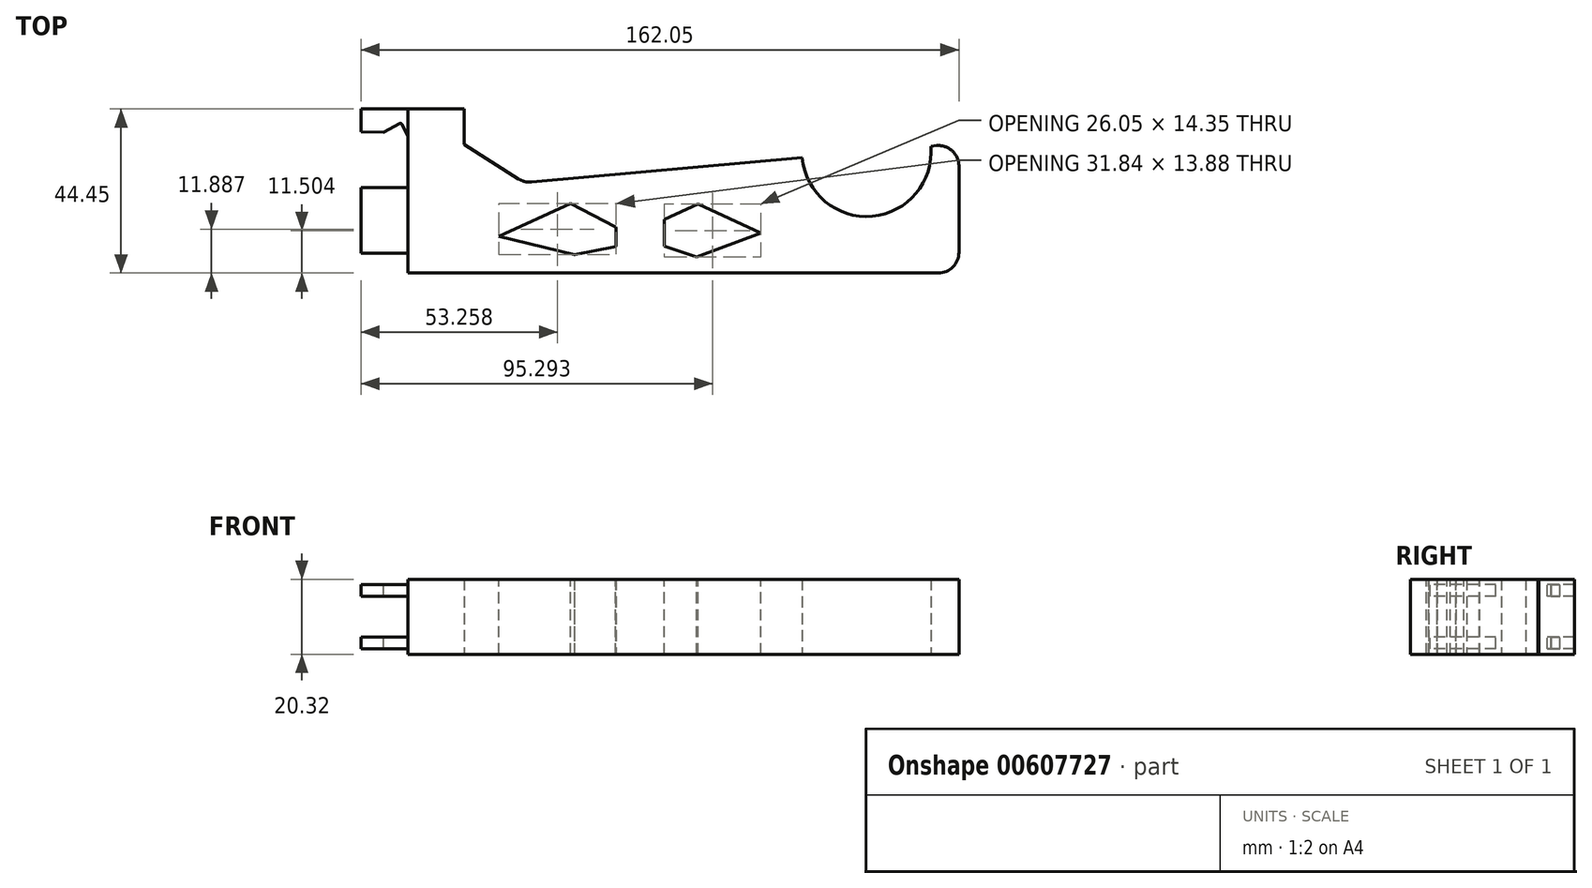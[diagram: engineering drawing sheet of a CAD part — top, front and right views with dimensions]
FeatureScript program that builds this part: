
annotation { "Feature Type Name" : "Feature", "Feature Type Description" : "" }
export const myFeature = defineFeature(function(context is Context, id is Id, definition is map)
    precondition{}
    {
        {
            var Q0;
            Q0=qCreatedBy(makeId("Top.planeOp"),FACE);
            var sketch = newSketch(context, id + "F0", { "sketchPlane" : qUnion([Q0])});
            skLineSegment(sketch, "E0", {"start": v(0, 0) * mm, "end": v(0, -44.45) * mm});
            skLineSegment(sketch, "E1", {"start": v(0, -44.45) * mm, "end": v(143.76, -44.45) * mm});
            skLineSegment(sketch, "E2", {"start": v(149.35, -38.86) * mm, "end": v(149.35, -15.5) * mm});
            skLineSegment(sketch, "E3", {"start": v(143.26, -9.94) * mm, "end": v(141.73, -10.08) * mm});
            skLineSegment(sketch, "E4", {"start": v(30.06, -18.98) * mm, "end": v(15.23, -9.62) * mm});
            skPoint(sketch, "E5", {"position": v(149.35, -9.4) * mm});
            skPoint(sketch, "E6", {"position": v(149.35, 0) * mm});
            skArc(sketch, "E7", {"start": v(106.9, -13.22) * mm, "mid": v(125.88, -29.07) * mm, "end": v(141.73, -10.08) * mm});
            skLineSegment(sketch, "E8.trimOffspring", {"start": v(106.9, -13.22) * mm, "end": v(33.55, -19.82) * mm});
            skPoint(sketch, "E9.visualSharp", {"position": v(31.66, -20) * mm});
            skArc(sketch, "E9.filletArc", {"start": v(30.06, -18.98) * mm, "mid": v(31.73, -19.69) * mm, "end": v(33.55, -19.82) * mm});
            skArc(sketch, "E10.filletArc", {"start": v(149.35, -15.5) * mm, "mid": v(147.53, -11.38) * mm, "end": v(143.26, -9.94) * mm});
            skPoint(sketch, "E11.visualSharp", {"position": v(149.35, -44.45) * mm});
            skArc(sketch, "E11.filletArc", {"start": v(143.76, -44.45) * mm, "mid": v(147.72, -42.81) * mm, "end": v(149.35, -38.86) * mm});
            skLineSegment(sketch, "E12", {"start": v(0, 0) * mm, "end": v(15.23, 0) * mm});
            skLineSegment(sketch, "E13", {"start": v(15.23, 0) * mm, "end": v(15.23, -9.62) * mm});
            skSolve(sketch);
        }
        {
            var Q0;
            Q0 = qSketchRegion(id + "F0", true);
            extrude(context, id + "F1", {"entities" : qUnion([Q0]), "depth" : 20.32 * mm, "offsetDistance" : 25.4 * mm});
        }
        {
            var Q0;
            Q0=makeQuery(id+"F1.opExtrude","SWEPT_FACE",FACE,{"disambiguationData":[OSD([sQuery(id+"F0.wireOp",EDGE,"E0")])]});
            var sketch = newSketch(context, id + "F2", { "sketchPlane" : qUnion([Q0])});
            skLineSegment(sketch, "E14", {"start": v(0, 10.16) * mm, "end": v(44.45, 10.16) * mm});
            skLineSegment(sketch, "E15.0", {"start": v(0, 4.6) * mm, "end": v(44.45, 4.6) * mm});
            skLineSegment(sketch, "E16.0", {"start": v(0, 1.43) * mm, "end": v(44.45, 1.43) * mm});
            skLineSegment(sketch, "E17.MirrorCS", {"start": v(0, 15.72) * mm, "end": v(44.45, 15.72) * mm});
            skLineSegment(sketch, "E18.MirrorCS", {"start": v(0, 18.9) * mm, "end": v(44.45, 18.9) * mm});
            skSolve(sketch);
        }
        {
            var Q0;
            Q0 = qSketchRegion(id + "F2", true);
            var Q1;
            {var subQ0=sQuery(id+"F2.wireOp",EDGE,"E15.0");Q1=makeQuery(id+"F2.imprint","IMPRINT",FACE,{"disambiguationData":[TD([[makeQuery(id+"F2.imprint","IMPRINT",EDGE,{"derivedFrom":subQ0}),-1.0]])]});}
            var Q2;
            {var subQ0=sQuery(id+"F2.wireOp",EDGE,"E17.MirrorCS");Q2=makeQuery(id+"F2.imprint","IMPRINT",FACE,{"disambiguationData":[TD([[makeQuery(id+"F2.imprint","IMPRINT",EDGE,{"derivedFrom":subQ0}),1.0]])]});}
            extrude(context, id + "F3", {"entities" : qUnion([Q0, Q1, Q2]), "operationType" : NewBodyOperationType.ADD, "depth" : 12.7 * mm, "offsetDistance" : 25.4 * mm});
        }
        {
            var Q0;
            Q0=makeQuery(id+"F3.opExtrude","SWEPT_FACE",FACE,{"disambiguationData":[OSD([sQuery(id+"F2.wireOp",EDGE,"E18.MirrorCS")])]});
            var sketch = newSketch(context, id + "F4", { "sketchPlane" : qUnion([Q0])});
            skLineSegment(sketch, "E19", {"start": v(-12.7, -21.26) * mm, "end": v(0, -21.26) * mm});
            skLineSegment(sketch, "E20.0", {"start": v(-12.7, -7.3) * mm, "end": v(0, -7.3) * mm});
            skLineSegment(sketch, "E21", {"start": v(-12.7, -21.26) * mm, "end": v(-12.7, -7.3) * mm});
            skLineSegment(sketch, "E22", {"start": v(0, -7.3) * mm, "end": v(0, -21.26) * mm});
            skLineSegment(sketch, "E23.0", {"start": v(-12.7, -39.04) * mm, "end": v(0, -39.04) * mm});
            skLineSegment(sketch, "E24", {"start": v(-12.7, -39.04) * mm, "end": v(-12.7, -44.45) * mm});
            skLineSegment(sketch, "E25", {"start": v(-12.23, -44.68) * mm, "end": v(0, -44.45) * mm});
            skLineSegment(sketch, "E26", {"start": v(0, -44.45) * mm, "end": v(0, -39.04) * mm});
            skLineSegment(sketch, "E27", {"start": v(0, 0) * mm, "end": v(-12.7, 0) * mm});
            skLineSegment(sketch, "E28", {"start": v(-12.7, 0) * mm, "end": v(-12.7, -6.22) * mm});
            skLineSegment(sketch, "E29", {"start": v(-12.7, -6.22) * mm, "end": v(-6.6, -6.28) * mm});
            skLineSegment(sketch, "E30", {"start": v(-6.6, -6.28) * mm, "end": v(-2.11, -3.97) * mm});
            skLineSegment(sketch, "E31", {"start": v(-1.6, -4.13) * mm, "end": v(0, -7.3) * mm});
            skPoint(sketch, "E32.visualSharp", {"position": v(-1.78, -3.8) * mm});
            skArc(sketch, "E32.filletArc", {"start": v(-1.6, -4.13) * mm, "mid": v(-1.83, -3.94) * mm, "end": v(-2.11, -3.97) * mm});
            skLineSegment(sketch, "E33", {"start": v(-12.7, -7.3) * mm, "end": v(-12.7, -6.22) * mm});
            skSolve(sketch);
        }
        {
            var Q0;
            Q0 = qSketchRegion(id + "F4", true);
            var Q1;
            Q1=makeQuery(id+"F4.imprint","IMPRINT",FACE,{"disambiguationData":[TD([[makeQuery(id+"F4.imprint","IMPRINT",EDGE,{"derivedFrom":sQuery(id+"F4.wireOp",EDGE,"E23.0")}),-1.0]])]});
            var Q2;
            Q2=makeQuery(id+"F3.opExtrude","SWEPT_FACE",FACE,{"disambiguationData":[OSD([sQuery(id+"F2.wireOp",EDGE,"E16.0")])]});
            extrude(context, id + "F5", {"entities" : qUnion([Q0, Q1]), "operationType" : NewBodyOperationType.REMOVE, "endBound" : BoundingType.UP_TO_SURFACE, "oppositeDirection" : true, "depth" : 25.4 * mm, "endBoundEntityFace" : qUnion([Q2]), "offsetDistance" : 25.4 * mm});
        }
        {
            var Q0;
            Q0=makeQuery(id+"F1.opExtrude","CAP_FACE",FACE,{"disambiguationData":[OSD([sQuery(id+"F0.wireOp",EDGE,"E0"),sQuery(id+"F0.wireOp",EDGE,"E1"),sQuery(id+"F0.wireOp",EDGE,"E2"),sQuery(id+"F0.wireOp",EDGE,"E3"),sQuery(id+"F0.wireOp",EDGE,"E4"),sQuery(id+"F0.wireOp",EDGE,"E7"),sQuery(id+"F0.wireOp",EDGE,"E8.trimOffspring"),sQuery(id+"F0.wireOp",EDGE,"E9.filletArc"),sQuery(id+"F0.wireOp",EDGE,"E10.filletArc"),sQuery(id+"F0.wireOp",EDGE,"E11.filletArc"),sQuery(id+"F0.wireOp",EDGE,"E12"),sQuery(id+"F0.wireOp",EDGE,"E13")])],"isStart":false});
            var sketch = newSketch(context, id + "F6", { "sketchPlane" : qUnion([Q0])});
            skLineSegment(sketch, "E34", {"start": v(24.64, -34.53) * mm, "end": v(44.12, -25.62) * mm});
            skLineSegment(sketch, "E35", {"start": v(44.12, -25.62) * mm, "end": v(60.43, -34.08) * mm});
            skLineSegment(sketch, "E36", {"start": v(60.43, -34.08) * mm, "end": v(78.7, -25.77) * mm});
            skLineSegment(sketch, "E37", {"start": v(78.7, -25.77) * mm, "end": v(95.62, -33.63) * mm});
            skLineSegment(sketch, "E38", {"start": v(95.62, -33.63) * mm, "end": v(78.25, -40.12) * mm});
            skLineSegment(sketch, "E39", {"start": v(78.25, -40.12) * mm, "end": v(60.43, -34.08) * mm});
            skLineSegment(sketch, "E40", {"start": v(24.64, -34.53) * mm, "end": v(45.18, -39.52) * mm});
            skLineSegment(sketch, "E41", {"start": v(45.18, -39.52) * mm, "end": v(65, -35.63) * mm});
            skLineSegment(sketch, "E42", {"start": v(56.48, -32.03) * mm, "end": v(56.48, -37.3) * mm});
            skLineSegment(sketch, "E43", {"start": v(56.48, -37.3) * mm, "end": v(69.57, -29.93) * mm});
            skLineSegment(sketch, "E44", {"start": v(69.57, -29.93) * mm, "end": v(69.57, -37.18) * mm});
            skSolve(sketch);
        }
        {
            var Q0;
            Q0=makeQuery(id+"F6.imprint","IMPRINT",FACE,{"disambiguationData":[TD([[makeQuery(id+"F6.imprint","IMPRINT",EDGE,{"derivedFrom":sQuery(id+"F6.wireOp",EDGE,"E34")}),-1.0]])]});
            var Q1;
            {var subQ3=sQuery(id+"F6.wireOp",EDGE,"E37");Q1=makeQuery(id+"F6.imprint","IMPRINT",FACE,{"disambiguationData":[TD([[makeQuery(id+"F6.imprint","IMPRINT",EDGE,{"derivedFrom":subQ3}),-1.0]])]});}
            extrude(context, id + "F7", {"entities" : qUnion([Q0, Q1]), "operationType" : NewBodyOperationType.REMOVE, "endBound" : BoundingType.UP_TO_NEXT, "oppositeDirection" : true, "depth" : 25.4 * mm, "offsetDistance" : 25.4 * mm});
        }
        {
            var Q0;
            Q0=makeQuery(id+"F7.boolean.opBoolean","COPY",EDGE,{"derivedFrom":makeQuery(id+"F7.opExtrude","CAP_EDGE",EDGE,{"disambiguationData":[OSD([sQuery(id+"F6.wireOp",EDGE,"E42")])],"isStart":true})});
            var Q1;
            Q1=makeQuery(id+"F7.boolean.opBoolean","COPY",EDGE,{"derivedFrom":makeQuery(id+"F7.opExtrude","SWEPT_EDGE",EDGE,{"disambiguationData":[OSD([sQuery(id+"F6.wireOp",EDGE,"E35"),sQuery(id+"F6.wireOp",EDGE,"E42")])]})});
            var Q2;
            Q2=makeQuery(id+"F7.boolean.opBoolean","COPY",EDGE,{"derivedFrom":makeQuery(id+"F7.opExtrude","SWEPT_EDGE",EDGE,{"disambiguationData":[OSD([sQuery(id+"F6.wireOp",EDGE,"E41"),sQuery(id+"F6.wireOp",EDGE,"E42"),sQuery(id+"F6.wireOp",EDGE,"E43")])]})});
            var Q3;
            Q3=makeQuery(id+"F7.boolean.opBoolean","COPY",EDGE,{"derivedFrom":makeQuery(id+"F7.opExtrude","CAP_EDGE",EDGE,{"disambiguationData":[OSD([sQuery(id+"F6.wireOp",EDGE,"E41")])],"isStart":true})});
            var Q4;
            Q4=makeQuery(id+"F7.boolean.opBoolean","COPY",EDGE,{"derivedFrom":makeQuery(id+"F7.opExtrude","CAP_EDGE",EDGE,{"disambiguationData":[OSD([sQuery(id+"F6.wireOp",EDGE,"E42")])],"isStart":false})});
            var Q5;
            Q5=makeQuery(id+"F7.boolean.opBoolean","COPY",EDGE,{"derivedFrom":makeQuery(id+"F7.opExtrude","CAP_EDGE",EDGE,{"disambiguationData":[OSD([sQuery(id+"F6.wireOp",EDGE,"E41")])],"isStart":false})});
            var Q6;
            Q6=makeQuery(id+"F7.boolean.opBoolean","COPY",EDGE,{"derivedFrom":makeQuery(id+"F7.opExtrude","SWEPT_EDGE",EDGE,{"disambiguationData":[OSD([sQuery(id+"F6.wireOp",EDGE,"E40"),sQuery(id+"F6.wireOp",EDGE,"E41")])]})});
            var Q7;
            Q7=makeQuery(id+"F7.boolean.opBoolean","COPY",EDGE,{"derivedFrom":makeQuery(id+"F7.opExtrude","CAP_EDGE",EDGE,{"disambiguationData":[OSD([sQuery(id+"F6.wireOp",EDGE,"E40")])],"isStart":true})});
            var Q8;
            Q8=makeQuery(id+"F7.boolean.opBoolean","COPY",EDGE,{"derivedFrom":makeQuery(id+"F7.opExtrude","CAP_EDGE",EDGE,{"disambiguationData":[OSD([sQuery(id+"F6.wireOp",EDGE,"E34")])],"isStart":true})});
            var Q9;
            Q9=makeQuery(id+"F7.boolean.opBoolean","COPY",EDGE,{"derivedFrom":makeQuery(id+"F7.opExtrude","CAP_EDGE",EDGE,{"disambiguationData":[OSD([sQuery(id+"F6.wireOp",EDGE,"E35")])],"isStart":true})});
            chamfer(context, id + "F8", {"entities" : qUnion([Q0, Q1, Q2, Q3, Q4, Q5, Q6, Q7, Q8, Q9]), "width" : 0.25 * mm, "tangentPropagation" : true});
        }
    });
